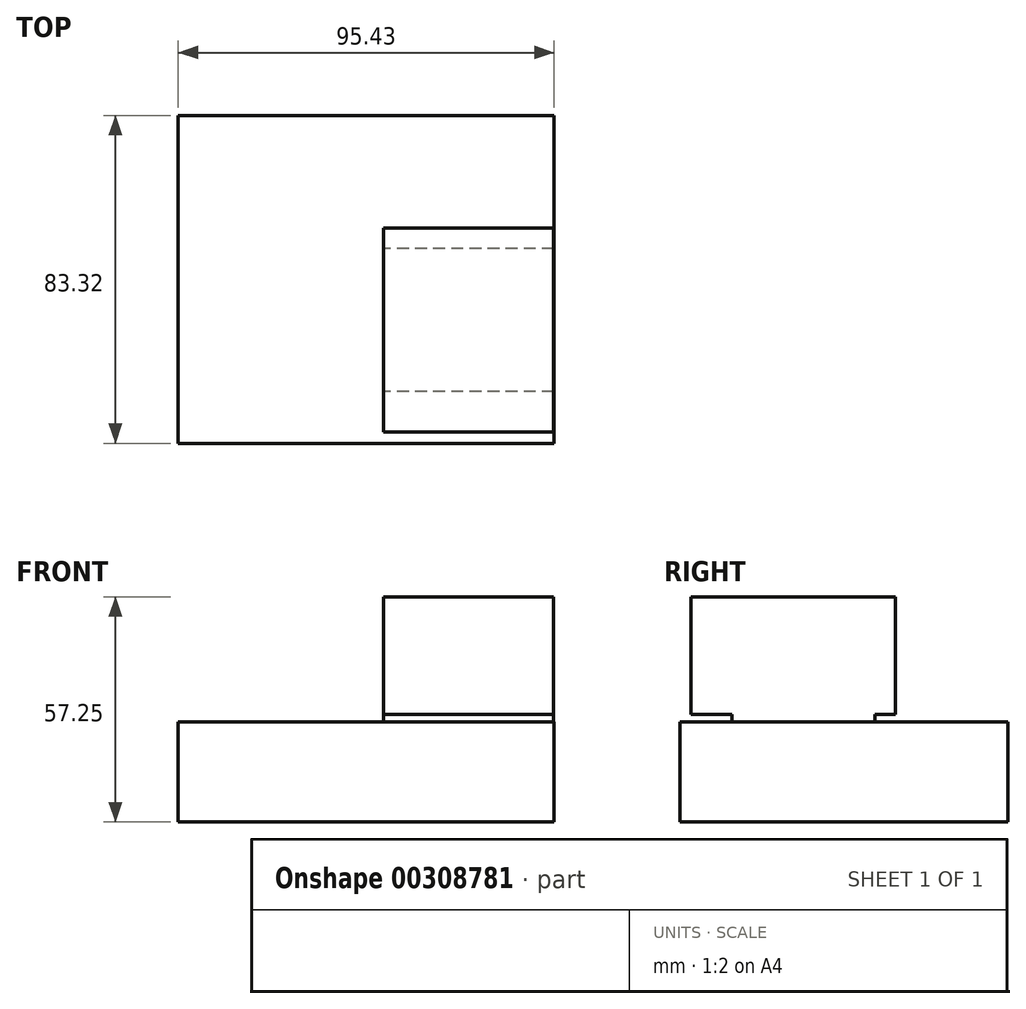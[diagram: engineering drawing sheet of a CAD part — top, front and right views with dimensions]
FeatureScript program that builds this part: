
annotation { "Feature Type Name" : "Feature", "Feature Type Description" : "" }
export const myFeature = defineFeature(function(context is Context, id is Id, definition is map)
    precondition{}
    {
        {
            var Q0;
            Q0=qCreatedBy(makeId("Top.planeOp"),FACE);
            var sketch = newSketch(context, id + "F0", { "sketchPlane" : qUnion([Q0])});
            skLineSegment(sketch, "E0.bottom", {"start": v(-52.18, 40.14) * mm, "end": v(43.25, 40.14) * mm});
            skLineSegment(sketch, "E0.top", {"start": v(-52.18, -43.18) * mm, "end": v(43.25, -43.18) * mm});
            skLineSegment(sketch, "E0.left", {"start": v(-52.18, 40.14) * mm, "end": v(-52.18, -43.18) * mm});
            skLineSegment(sketch, "E0.right", {"start": v(43.25, 40.14) * mm, "end": v(43.25, -43.18) * mm});
            skSolve(sketch);
        }
        {
            var Q0;
            Q0 = qSketchRegion(id + "F0", true);
            extrude(context, id + "F1", {"entities" : qUnion([Q0]), "depth" : 25.4 * mm});
        }
        {
            var Q0;
            Q0=qCreatedBy(makeId("Right.planeOp"),FACE);
            var sketch = newSketch(context, id + "F2", { "sketchPlane" : qUnion([Q0])});
            skLineSegment(sketch, "E1.bottom", {"start": v(-40.35, 27.4) * mm, "end": v(11.52, 27.4) * mm});
            skLineSegment(sketch, "E1.top", {"start": v(-40.35, 57.25) * mm, "end": v(11.52, 57.25) * mm});
            skLineSegment(sketch, "E1.left", {"start": v(-40.35, 27.4) * mm, "end": v(-40.35, 57.25) * mm});
            skLineSegment(sketch, "E1.right", {"start": v(11.52, 27.4) * mm, "end": v(11.52, 57.25) * mm});
            skLineSegment(sketch, "E2.bottom", {"start": v(-29.96, 27.4) * mm, "end": v(6.34, 27.4) * mm});
            skLineSegment(sketch, "E2.top", {"start": v(-29.96, 10.75) * mm, "end": v(6.34, 10.75) * mm});
            skLineSegment(sketch, "E2.left", {"start": v(-29.96, 27.4) * mm, "end": v(-29.96, 10.75) * mm});
            skLineSegment(sketch, "E2.right", {"start": v(6.34, 27.4) * mm, "end": v(6.34, 10.75) * mm});
            skSolve(sketch);
        }
        {
            var Q0;
            Q0 = qSketchRegion(id + "F2", true);
            extrude(context, id + "F3", {"entities" : qUnion([Q0]), "operationType" : NewBodyOperationType.ADD, "depth" : 43.18 * mm});
        }
    });
